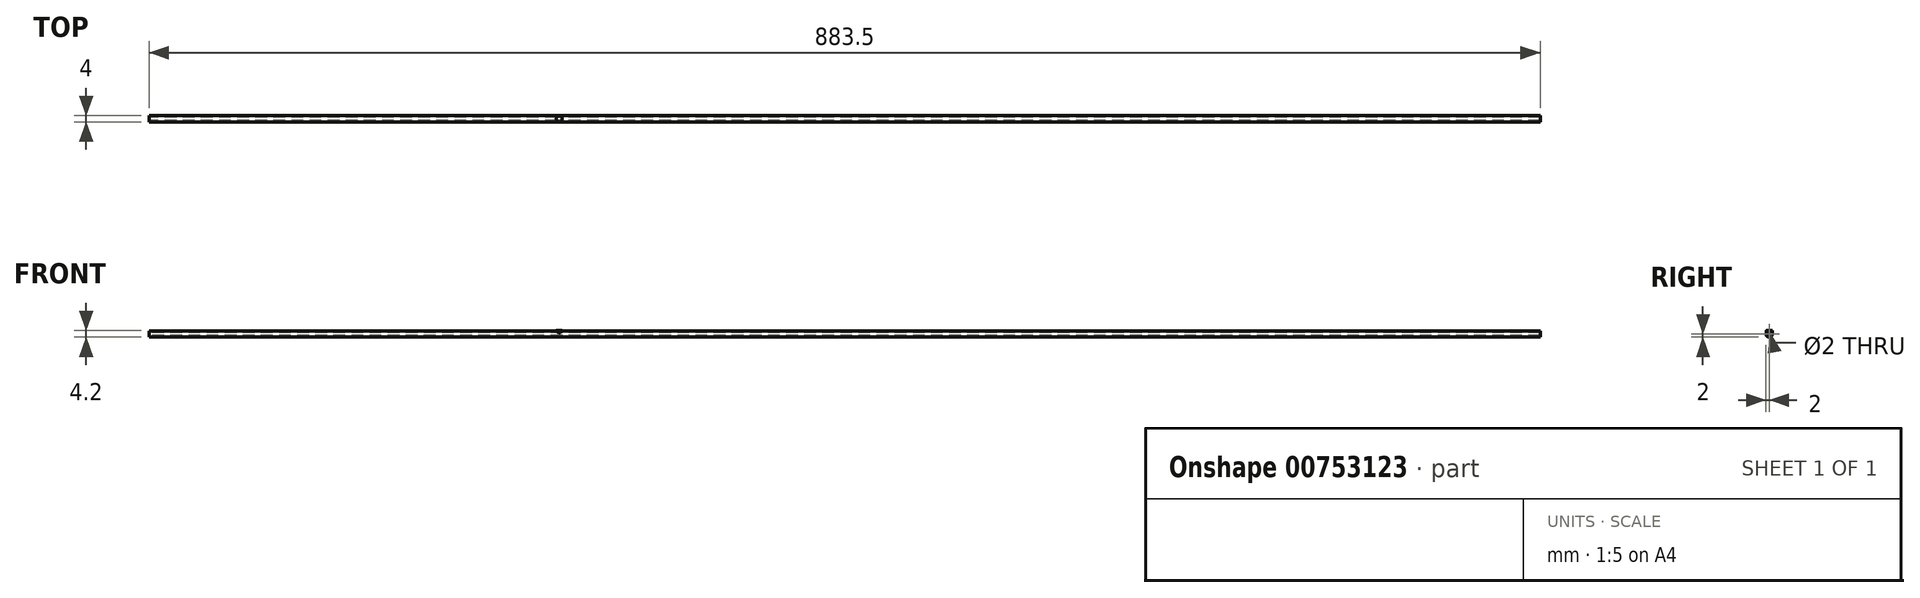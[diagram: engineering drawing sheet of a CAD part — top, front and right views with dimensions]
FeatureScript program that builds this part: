
annotation { "Feature Type Name" : "Feature", "Feature Type Description" : "" }
export const myFeature = defineFeature(function(context is Context, id is Id, definition is map)
    precondition{}
    {
        {
            var Q0;
            Q0=qCreatedBy(makeId("Right.planeOp"),FACE);
            var sketch = newSketch(context, id + "F0", { "sketchPlane" : qUnion([Q0])});
            skArc(sketch, "E0", {"start": v(-1.5, 1.32) * mm, "mid": v(0, -2) * mm, "end": v(1.5, 1.32) * mm});
            skCircle(sketch, "E1", {"center": v(0, 0) * mm, "radius": 1 * mm});
            skLineSegment(sketch, "E2", {"start": v(0, 0) * mm, "end": v(0, 2) * mm, "construction": true});
            skLineSegment(sketch, "E3", {"start": v(-1.5, 1.32) * mm, "end": v(1.5, 1.32) * mm, "construction": true});
            skArc(sketch, "E4", {"start": v(1.5, 1.32) * mm, "mid": v(0, 2) * mm, "end": v(-1.5, 1.32) * mm});
            skSolve(sketch);
        }
        {
            var Q0;
            Q0 = qSketchRegion(id + "F0", true);
            extrude(context, id + "F1", {"entities" : qUnion([Q0]), "depth" : 883.5 * mm, "offsetDistance" : 25 * mm});
        }
        {
            var Q0;
            Q0=qCreatedBy(makeId("Top.planeOp"),FACE);
            cPlane(context, id + "F2", {"entities" : qUnion([Q0]), "cplaneType" : CPlaneType.OFFSET, "offset" : 2.2 * mm, "width" : 150 * mm, "height" : 150 * mm});
        }
        {
            var Q0;
            Q0=qCreatedBy(id+"F2.planeOp",FACE);
            var sketch = newSketch(context, id + "F3", { "sketchPlane" : qUnion([Q0])});
            skCircle(sketch, "E5", {"center": v(260.47, 0) * mm, "radius": 1.9 * mm});
            skSolve(sketch);
        }
        {
            var Q0;
            Q0 = qSketchRegion(id + "F3", true);
            var Q1;
            Q1=makeQuery(id+"F1.opExtrude","SWEPT_FACE",FACE,{"disambiguationData":[OSD([sQuery(id+"F0.wireOp",EDGE,"E0"),sQuery(id+"F0.wireOp",EDGE,"E4")])]});
            var Q2;
            Q2=makeQuery(id+"F1.opExtrude","SWEPT_BODY",BODY,{"disambiguationData":[OSD([sQuery(id+"F0.wireOp",EDGE,"E0"),sQuery(id+"F0.wireOp",EDGE,"E1"),sQuery(id+"F0.wireOp",EDGE,"E4")])]});
            extrude(context, id + "F4", {"entities" : qUnion([Q0]), "operationType" : NewBodyOperationType.ADD, "endBound" : BoundingType.UP_TO_BODY, "oppositeDirection" : true, "depth" : 25 * mm, "endBoundEntityFace" : qUnion([Q1]), "endBoundEntityBody" : qUnion([Q2]), "offsetDistance" : 25 * mm});
        }
    });
